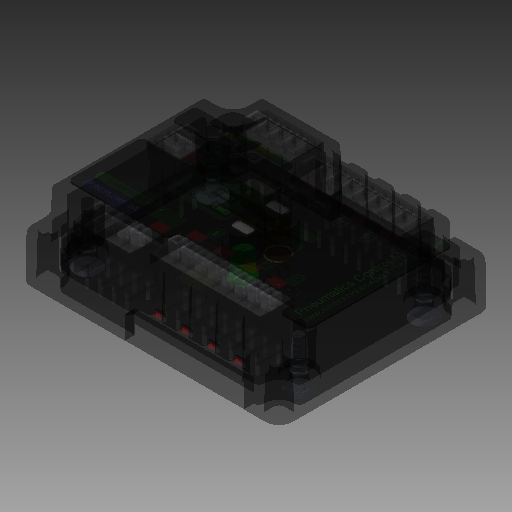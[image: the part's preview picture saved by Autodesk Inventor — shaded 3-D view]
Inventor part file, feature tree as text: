
AUTODESK INVENTOR PART (.ipt)
format: ipt  version: 2019 (Build 230136000, 136)  size: 13,045,248 bytes
history: native  units: in
note: dims shown in document units (in); Inventor stores cm internally (conversion verified against a paired STEP export)
features: other x3, sketch x1
ambient origin geometry x8: Origin, YZ Plane, XZ Plane, XY Plane, X Axis, Y Axis, Z Axis, Center Point
bodies: Body1 (feature_tree), Body2 (feature_tree), Body3 (feature_tree), Body4 (feature_tree), Body5 (feature_tree), Body6 (feature_tree), Body7 (feature_tree), Body8 (feature_tree), Body9 (feature_tree), Body10 (feature_tree), Body11 (feature_tree), Body12 (feature_tree), Body13 (feature_tree), Body14 (feature_tree), Body15 (feature_tree), Body16 (feature_tree), Body17 (feature_tree), Body18 (feature_tree), Body19 (feature_tree), Body20 (feature_tree), Body21 (feature_tree), Body22 (feature_tree), Body23 (feature_tree), Body24 (feature_tree)
feature tree (4):
  other  "pneumatic control1"
  sketch  "Sketch1"  dims[d0=1.923in d1=2.403in]
  other  "Composite1"
  other  "Srf1"
